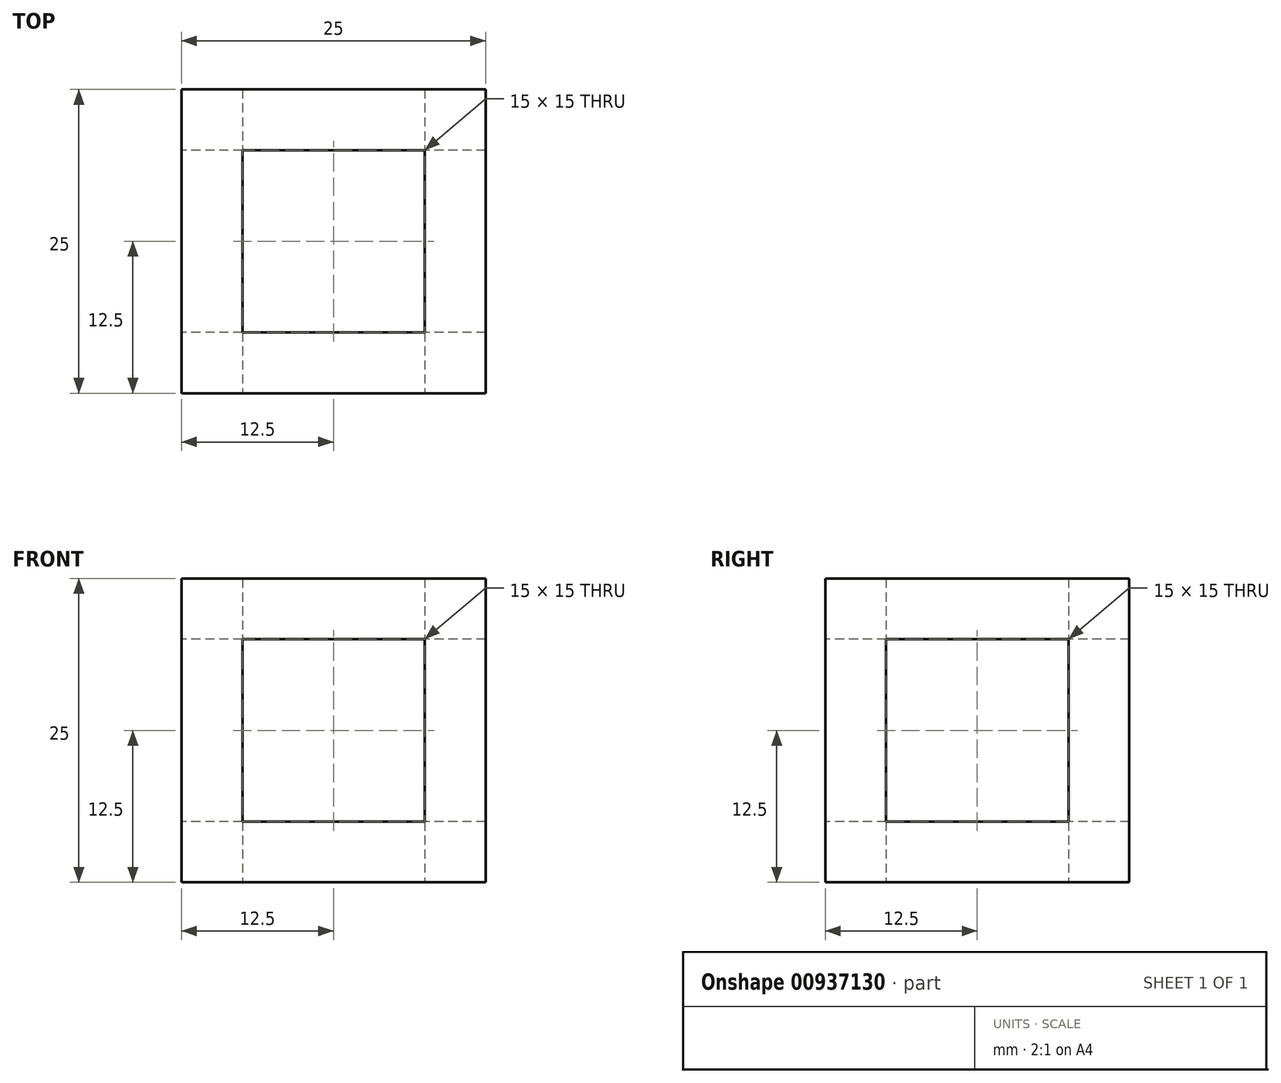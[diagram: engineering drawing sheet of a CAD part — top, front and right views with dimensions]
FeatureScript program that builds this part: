
annotation { "Feature Type Name" : "Feature", "Feature Type Description" : "" }
export const myFeature = defineFeature(function(context is Context, id is Id, definition is map)
    precondition{}
    {
        {
            var Q0;
            Q0=qCreatedBy(makeId("Top.planeOp"),FACE);
            var sketch = newSketch(context, id + "F0", { "sketchPlane" : qUnion([Q0])});
            skLineSegment(sketch, "E0.bottom", {"start": v(-7.5, 7.5) * mm, "end": v(7.5, 7.5) * mm});
            skLineSegment(sketch, "E0.top", {"start": v(-7.5, -7.5) * mm, "end": v(7.5, -7.5) * mm});
            skLineSegment(sketch, "E0.left", {"start": v(-7.5, 7.5) * mm, "end": v(-7.5, -7.5) * mm});
            skLineSegment(sketch, "E0.right", {"start": v(7.5, 7.5) * mm, "end": v(7.5, -7.5) * mm});
            skPoint(sketch, "E0.middle", {"position": v(0, 0) * mm});
            skLineSegment(sketch, "E1.bottom", {"start": v(-12.5, 12.5) * mm, "end": v(12.5, 12.5) * mm});
            skLineSegment(sketch, "E1.top", {"start": v(-12.5, -12.5) * mm, "end": v(12.5, -12.5) * mm});
            skLineSegment(sketch, "E1.left", {"start": v(-12.5, 12.5) * mm, "end": v(-12.5, -12.5) * mm});
            skLineSegment(sketch, "E1.right", {"start": v(12.5, 12.5) * mm, "end": v(12.5, -12.5) * mm});
            skSolve(sketch);
        }
        {
            var Q0;
            Q0=makeQuery(id+"F0.imprint","IMPRINT",FACE,{"disambiguationData":[TD([[makeQuery(id+"F0.imprint","IMPRINT",EDGE,{"derivedFrom":sQuery(id+"F0.wireOp",EDGE,"E0.bottom")}),1.0]])]});
            extrude(context, id + "F1", {"entities" : qUnion([Q0]), "depth" : 25 * mm, "offsetDistance" : 25 * mm});
        }
        {
            var Q0;
            Q0=makeQuery(id+"F1.opExtrude","SWEPT_FACE",FACE,{"disambiguationData":[OSD([sQuery(id+"F0.wireOp",EDGE,"E1.left")])]});
            var sketch = newSketch(context, id + "F2", { "sketchPlane" : qUnion([Q0])});
            skLineSegment(sketch, "E2.bottom", {"start": v(-7.5, 20) * mm, "end": v(7.5, 20) * mm});
            skLineSegment(sketch, "E2.top", {"start": v(-7.5, 5) * mm, "end": v(7.5, 5) * mm});
            skLineSegment(sketch, "E2.left", {"start": v(-7.5, 20) * mm, "end": v(-7.5, 5) * mm});
            skLineSegment(sketch, "E2.right", {"start": v(7.5, 20) * mm, "end": v(7.5, 5) * mm});
            skPoint(sketch, "E2.middle", {"position": v(0, 12.5) * mm});
            skSolve(sketch);
        }
        {
            var Q0;
            Q0=makeQuery(id+"F2.imprint","IMPRINT",FACE,{"disambiguationData":[TD([[makeQuery(id+"F2.imprint","IMPRINT",EDGE,{"derivedFrom":sQuery(id+"F2.wireOp",EDGE,"E2.bottom")}),-1.0]])]});
            extrude(context, id + "F3", {"entities" : qUnion([Q0]), "operationType" : NewBodyOperationType.REMOVE, "endBound" : BoundingType.THROUGH_ALL, "oppositeDirection" : true, "depth" : 25 * mm, "offsetDistance" : 25 * mm});
        }
        {
            var Q0;
            Q0=makeQuery(id+"F1.opExtrude","SWEPT_FACE",FACE,{"disambiguationData":[OSD([sQuery(id+"F0.wireOp",EDGE,"E1.top")])]});
            var sketch = newSketch(context, id + "F4", { "sketchPlane" : qUnion([Q0])});
            skLineSegment(sketch, "E3.bottom", {"start": v(-7.5, 20) * mm, "end": v(7.5, 20) * mm});
            skLineSegment(sketch, "E3.top", {"start": v(-7.5, 5) * mm, "end": v(7.5, 5) * mm});
            skLineSegment(sketch, "E3.left", {"start": v(-7.5, 20) * mm, "end": v(-7.5, 5) * mm});
            skLineSegment(sketch, "E3.right", {"start": v(7.5, 20) * mm, "end": v(7.5, 5) * mm});
            skPoint(sketch, "E3.middle", {"position": v(0, 12.5) * mm});
            skSolve(sketch);
        }
        {
            var Q0;
            Q0=makeQuery(id+"F4.imprint","IMPRINT",FACE,{"disambiguationData":[TD([[makeQuery(id+"F4.imprint","IMPRINT",EDGE,{"derivedFrom":sQuery(id+"F4.wireOp",EDGE,"E3.bottom")}),-1.0]])]});
            extrude(context, id + "F5", {"entities" : qUnion([Q0]), "operationType" : NewBodyOperationType.REMOVE, "oppositeDirection" : true, "depth" : 25 * mm, "offsetDistance" : 25 * mm});
        }
    });
